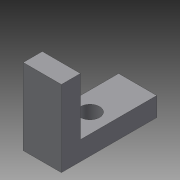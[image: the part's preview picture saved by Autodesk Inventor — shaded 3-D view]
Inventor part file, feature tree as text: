
AUTODESK INVENTOR PART (.ipt)
format: ipt  version: 2014 (Build 180170000, 170)  size: 87,040 bytes
history: native  units: mm
features: sketch x3, extrude x2, other x1, hole x1
ambient origin geometry x8: Origin, YZ Plane, XZ Plane, XY Plane, X Axis, Y Axis, Z Axis, Center Point
bodies: Body1 (feature_tree)
feature tree (7):
  other  "Твердое тело1"
  extrude  "Выдавливание1"  Depth=6.0mm
  hole  "Отверстие1"  [1 undecoded]
  extrude  "Выдавливание2"  Depth=3.0mm TaperAngle=0.0deg
  sketch  "Эскиз1"
  sketch  "Эскиз2"
  sketch  "Эскиз3"
note: 1 required parameter value undecoded (feature->parameter linkage not recoverable at this tier; creation-order binding heuristic only, values carry confidence <= 0.55)
